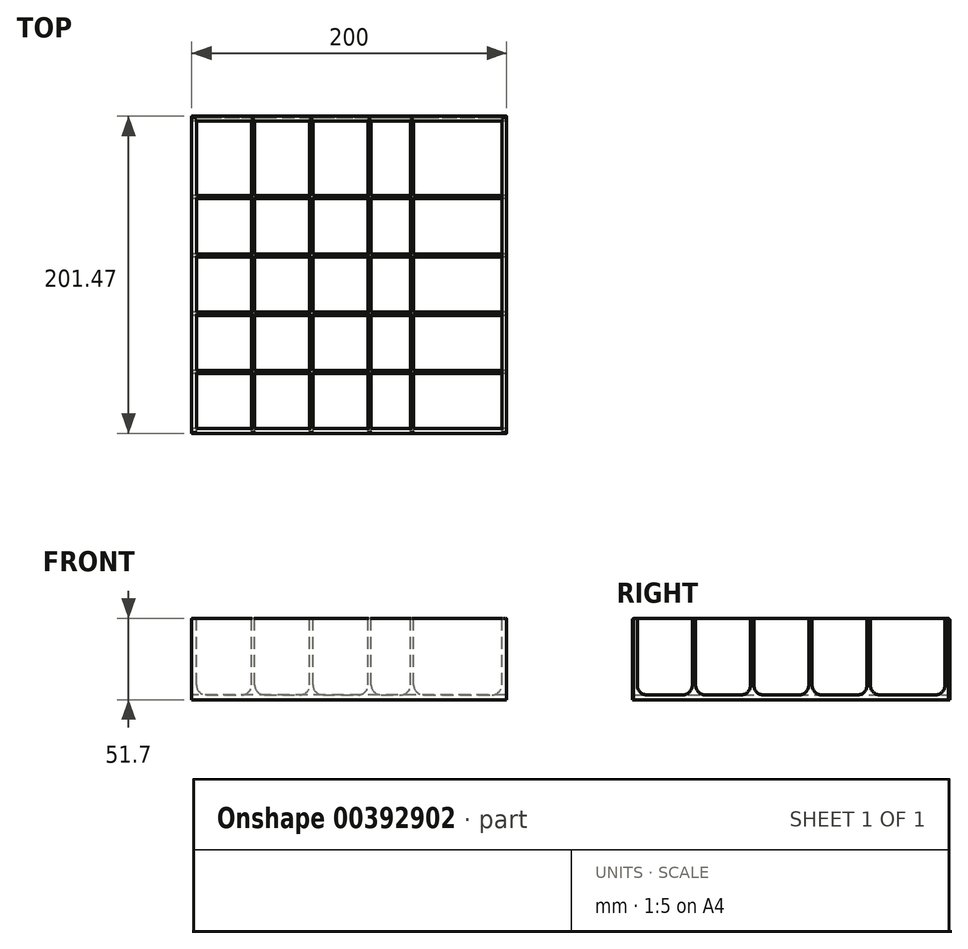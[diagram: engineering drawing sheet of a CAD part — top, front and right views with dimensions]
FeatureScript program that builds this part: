
annotation { "Feature Type Name" : "Feature", "Feature Type Description" : "" }
export const myFeature = defineFeature(function(context is Context, id is Id, definition is map)
    precondition{}
    {
        {
            var Q0;
            Q0=qCreatedBy(makeId("Front.planeOp"),FACE);
            var sketch = newSketch(context, id + "F0", { "sketchPlane" : qUnion([Q0])});
            skLineSegment(sketch, "E0.bottom", {"start": v(-90.65, -22.35) * mm, "end": v(-68.35, -22.35) * mm});
            skLineSegment(sketch, "E0.top", {"start": v(-100, -25.4) * mm, "end": v(100, -25.4) * mm});
            skLineSegment(sketch, "E1.top", {"start": v(-99.1, 26.3) * mm, "end": v(-97.9, 26.3) * mm});
            skLineSegment(sketch, "E1.left", {"start": v(-100, -25.4) * mm, "end": v(-100, 25.4) * mm});
            skLineSegment(sketch, "E1.right", {"start": v(-97, -16) * mm, "end": v(-97, 25.4) * mm});
            skLineSegment(sketch, "E2.top", {"start": v(99.1, 26.3) * mm, "end": v(97.9, 26.3) * mm});
            skLineSegment(sketch, "E2.left", {"start": v(100, -25.4) * mm, "end": v(100, 25.4) * mm});
            skLineSegment(sketch, "E2.right", {"start": v(97, -16) * mm, "end": v(97, 25.4) * mm});
            skLineSegment(sketch, "E3.top", {"start": v(-61.1, 26.3) * mm, "end": v(-60.9, 26.3) * mm});
            skLineSegment(sketch, "E3.left", {"start": v(-62, -16) * mm, "end": v(-62, 25.4) * mm});
            skLineSegment(sketch, "E3.right", {"start": v(-60, -16) * mm, "end": v(-60, 25.4) * mm});
            skLineSegment(sketch, "E4.top", {"start": v(-24.1, 26.3) * mm, "end": v(-23.9, 26.3) * mm});
            skLineSegment(sketch, "E4.left", {"start": v(-25, -16) * mm, "end": v(-25, 25.4) * mm});
            skLineSegment(sketch, "E4.right", {"start": v(-23, -16) * mm, "end": v(-23, 25.4) * mm});
            skLineSegment(sketch, "E5.top", {"start": v(12.9, 26.3) * mm, "end": v(13.1, 26.3) * mm});
            skLineSegment(sketch, "E5.left", {"start": v(12, -16) * mm, "end": v(12, 25.4) * mm});
            skLineSegment(sketch, "E5.right", {"start": v(14, -16) * mm, "end": v(14, 25.4) * mm});
            skLineSegment(sketch, "E6.top", {"start": v(39.9, 26.3) * mm, "end": v(40.1, 26.3) * mm});
            skLineSegment(sketch, "E6.left", {"start": v(39, -16) * mm, "end": v(39, 25.4) * mm});
            skLineSegment(sketch, "E6.right", {"start": v(41, -16) * mm, "end": v(41, 25.4) * mm});
            skArc(sketch, "E7.filletArc", {"start": v(-97, -16) * mm, "mid": v(-95.14, -20.49) * mm, "end": v(-90.65, -22.35) * mm});
            skArc(sketch, "E8.filletArc", {"start": v(-68.35, -22.35) * mm, "mid": v(-63.86, -20.49) * mm, "end": v(-62, -16) * mm});
            skLineSegment(sketch, "E9", {"start": v(-53.65, -22.35) * mm, "end": v(-31.35, -22.35) * mm});
            skArc(sketch, "E10.filletArc", {"start": v(-60, -16) * mm, "mid": v(-58.14, -20.49) * mm, "end": v(-53.65, -22.35) * mm});
            skArc(sketch, "E11.filletArc", {"start": v(-31.35, -22.35) * mm, "mid": v(-26.86, -20.49) * mm, "end": v(-25, -16) * mm});
            skLineSegment(sketch, "E12", {"start": v(20.35, -22.35) * mm, "end": v(32.65, -22.35) * mm});
            skLineSegment(sketch, "E13", {"start": v(47.35, -22.35) * mm, "end": v(90.65, -22.35) * mm});
            skLineSegment(sketch, "E14", {"start": v(-16.65, -22.35) * mm, "end": v(5.65, -22.35) * mm});
            skArc(sketch, "E15.filletArc", {"start": v(-23, -16) * mm, "mid": v(-21.14, -20.49) * mm, "end": v(-16.65, -22.35) * mm});
            skArc(sketch, "E16.filletArc", {"start": v(5.65, -22.35) * mm, "mid": v(10.14, -20.49) * mm, "end": v(12, -16) * mm});
            skArc(sketch, "E17.filletArc", {"start": v(14, -16) * mm, "mid": v(15.86, -20.49) * mm, "end": v(20.35, -22.35) * mm});
            skArc(sketch, "E18.filletArc", {"start": v(32.65, -22.35) * mm, "mid": v(37.14, -20.49) * mm, "end": v(39, -16) * mm});
            skArc(sketch, "E19.filletArc", {"start": v(41, -16) * mm, "mid": v(42.86, -20.49) * mm, "end": v(47.35, -22.35) * mm});
            skArc(sketch, "E20.filletArc", {"start": v(90.65, -22.35) * mm, "mid": v(95.14, -20.49) * mm, "end": v(97, -16) * mm});
            skPoint(sketch, "E21.visualSharp", {"position": v(-100, 26.3) * mm});
            skArc(sketch, "E21.filletArc", {"start": v(-99.1, 26.3) * mm, "mid": v(-99.74, 26.04) * mm, "end": v(-100, 25.4) * mm});
            skPoint(sketch, "E22.visualSharp", {"position": v(-97, 26.3) * mm});
            skArc(sketch, "E22.filletArc", {"start": v(-97, 25.4) * mm, "mid": v(-97.26, 26.04) * mm, "end": v(-97.9, 26.3) * mm});
            skPoint(sketch, "E23.visualSharp", {"position": v(-62, 26.3) * mm});
            skArc(sketch, "E23.filletArc", {"start": v(-61.1, 26.3) * mm, "mid": v(-61.74, 26.04) * mm, "end": v(-62, 25.4) * mm});
            skPoint(sketch, "E24.visualSharp", {"position": v(-60, 26.3) * mm});
            skArc(sketch, "E24.filletArc", {"start": v(-60, 25.4) * mm, "mid": v(-60.26, 26.04) * mm, "end": v(-60.9, 26.3) * mm});
            skPoint(sketch, "E25.visualSharp", {"position": v(-25, 26.3) * mm});
            skArc(sketch, "E25.filletArc", {"start": v(-24.1, 26.3) * mm, "mid": v(-24.74, 26.04) * mm, "end": v(-25, 25.4) * mm});
            skPoint(sketch, "E26.visualSharp", {"position": v(-23, 26.3) * mm});
            skArc(sketch, "E26.filletArc", {"start": v(-23, 25.4) * mm, "mid": v(-23.26, 26.04) * mm, "end": v(-23.9, 26.3) * mm});
            skPoint(sketch, "E27.visualSharp", {"position": v(12, 26.3) * mm});
            skArc(sketch, "E27.filletArc", {"start": v(12.9, 26.3) * mm, "mid": v(12.26, 26.04) * mm, "end": v(12, 25.4) * mm});
            skPoint(sketch, "E28.visualSharp", {"position": v(14, 26.3) * mm});
            skArc(sketch, "E28.filletArc", {"start": v(14, 25.4) * mm, "mid": v(13.74, 26.04) * mm, "end": v(13.1, 26.3) * mm});
            skPoint(sketch, "E29.visualSharp", {"position": v(39, 26.3) * mm});
            skArc(sketch, "E29.filletArc", {"start": v(39.9, 26.3) * mm, "mid": v(39.26, 26.04) * mm, "end": v(39, 25.4) * mm});
            skPoint(sketch, "E30.visualSharp", {"position": v(41, 26.3) * mm});
            skArc(sketch, "E30.filletArc", {"start": v(41, 25.4) * mm, "mid": v(40.74, 26.04) * mm, "end": v(40.1, 26.3) * mm});
            skPoint(sketch, "E31.visualSharp", {"position": v(97, 26.3) * mm});
            skArc(sketch, "E31.filletArc", {"start": v(97.9, 26.3) * mm, "mid": v(97.26, 26.04) * mm, "end": v(97, 25.4) * mm});
            skArc(sketch, "E32.filletArc", {"start": v(100, 25.4) * mm, "mid": v(99.74, 26.04) * mm, "end": v(99.1, 26.3) * mm});
            skSolve(sketch);
        }
        {
            var Q0;
            Q0=qCreatedBy(makeId("Right.planeOp"),FACE);
            var sketch = newSketch(context, id + "F1", { "sketchPlane" : qUnion([Q0])});
            skLineSegment(sketch, "E33", {"start": v(99.33, -25.4) * mm, "end": v(-100.67, -25.4) * mm});
            skLineSegment(sketch, "E34", {"start": v(-100.67, -25.4) * mm, "end": v(-100.67, 25.4) * mm});
            skLineSegment(sketch, "E35", {"start": v(-99.9, 26.16) * mm, "end": v(-98.43, 26.16) * mm});
            skLineSegment(sketch, "E36", {"start": v(-97.67, 25.4) * mm, "end": v(-97.67, -16.05) * mm});
            skLineSegment(sketch, "E37", {"start": v(-91.32, -22.4) * mm, "end": v(-69.02, -22.4) * mm});
            skLineSegment(sketch, "E38", {"start": v(97.8, -16.05) * mm, "end": v(97.8, 25.4) * mm});
            skLineSegment(sketch, "E39", {"start": v(98.56, 26.16) * mm, "end": v(100.04, 26.16) * mm});
            skLineSegment(sketch, "E40", {"start": v(100.8, 25.4) * mm, "end": v(100.8, -25.4) * mm});
            skLineSegment(sketch, "E41", {"start": v(-62.67, -16.05) * mm, "end": v(-62.67, 25.4) * mm});
            skLineSegment(sketch, "E42", {"start": v(-61.9, 26.16) * mm, "end": v(-61.43, 26.16) * mm});
            skLineSegment(sketch, "E43", {"start": v(-60.67, 25.4) * mm, "end": v(-60.67, -16.05) * mm});
            skLineSegment(sketch, "E44.bottom", {"start": v(-24.9, 26.16) * mm, "end": v(-24.43, 26.16) * mm});
            skLineSegment(sketch, "E44.top", {"start": v(-25.67, -22.4) * mm, "end": v(-23.67, -22.4) * mm});
            skLineSegment(sketch, "E44.left", {"start": v(-25.67, 25.4) * mm, "end": v(-25.67, -16.05) * mm});
            skLineSegment(sketch, "E44.right", {"start": v(-23.67, 25.4) * mm, "end": v(-23.67, -16.05) * mm});
            skLineSegment(sketch, "E45.bottom", {"start": v(12.1, 26.16) * mm, "end": v(12.57, 26.16) * mm});
            skLineSegment(sketch, "E45.top", {"start": v(11.33, -22.4) * mm, "end": v(13.33, -22.4) * mm});
            skLineSegment(sketch, "E45.left", {"start": v(11.33, 25.4) * mm, "end": v(11.33, -16.05) * mm});
            skLineSegment(sketch, "E45.right", {"start": v(13.33, 25.4) * mm, "end": v(13.33, -16.05) * mm});
            skLineSegment(sketch, "E46.bottom", {"start": v(49.1, 26.16) * mm, "end": v(49.57, 26.16) * mm});
            skLineSegment(sketch, "E46.left", {"start": v(48.33, 25.4) * mm, "end": v(48.33, -16.05) * mm});
            skLineSegment(sketch, "E46.right", {"start": v(50.33, 25.4) * mm, "end": v(50.33, -16.05) * mm});
            skPoint(sketch, "E47.visualSharp", {"position": v(-97.67, -22.4) * mm});
            skArc(sketch, "E47.filletArc", {"start": v(-97.67, -16.05) * mm, "mid": v(-95.81, -20.54) * mm, "end": v(-91.32, -22.4) * mm});
            skArc(sketch, "E48.filletArc", {"start": v(-69.02, -22.4) * mm, "mid": v(-64.53, -20.54) * mm, "end": v(-62.67, -16.05) * mm});
            skLineSegment(sketch, "E49", {"start": v(-54.32, -22.4) * mm, "end": v(-32.02, -22.4) * mm});
            skLineSegment(sketch, "E50", {"start": v(-17.32, -22.4) * mm, "end": v(4.98, -22.4) * mm});
            skLineSegment(sketch, "E51", {"start": v(56.68, -22.4) * mm, "end": v(91.45, -22.4) * mm});
            skLineSegment(sketch, "E52", {"start": v(19.68, -22.4) * mm, "end": v(41.98, -22.4) * mm});
            skPoint(sketch, "E53.visualSharp", {"position": v(-60.67, -22.4) * mm});
            skArc(sketch, "E53.filletArc", {"start": v(-60.67, -16.05) * mm, "mid": v(-58.81, -20.54) * mm, "end": v(-54.32, -22.4) * mm});
            skPoint(sketch, "E54.visualSharp", {"position": v(-25.67, -22.4) * mm});
            skArc(sketch, "E54.filletArc", {"start": v(-32.02, -22.4) * mm, "mid": v(-27.53, -20.54) * mm, "end": v(-25.67, -16.05) * mm});
            skPoint(sketch, "E55.visualSharp", {"position": v(-23.67, -22.4) * mm});
            skArc(sketch, "E55.filletArc", {"start": v(-23.67, -16.05) * mm, "mid": v(-21.81, -20.54) * mm, "end": v(-17.32, -22.4) * mm});
            skPoint(sketch, "E56.visualSharp", {"position": v(11.33, -22.4) * mm});
            skArc(sketch, "E56.filletArc", {"start": v(4.98, -22.4) * mm, "mid": v(9.47, -20.54) * mm, "end": v(11.33, -16.05) * mm});
            skPoint(sketch, "E57.visualSharp", {"position": v(13.33, -22.4) * mm});
            skArc(sketch, "E57.filletArc", {"start": v(13.33, -16.05) * mm, "mid": v(15.19, -20.54) * mm, "end": v(19.68, -22.4) * mm});
            skPoint(sketch, "E58.visualSharp", {"position": v(48.33, -22.4) * mm});
            skArc(sketch, "E58.filletArc", {"start": v(41.98, -22.4) * mm, "mid": v(46.47, -20.54) * mm, "end": v(48.33, -16.05) * mm});
            skPoint(sketch, "E59.visualSharp", {"position": v(50.33, -22.4) * mm});
            skArc(sketch, "E59.filletArc", {"start": v(50.33, -16.05) * mm, "mid": v(52.19, -20.54) * mm, "end": v(56.68, -22.4) * mm});
            skPoint(sketch, "E60.visualSharp", {"position": v(97.8, -22.4) * mm});
            skArc(sketch, "E60.filletArc", {"start": v(91.45, -22.4) * mm, "mid": v(95.94, -20.54) * mm, "end": v(97.8, -16.05) * mm});
            skPoint(sketch, "E61.visualSharp", {"position": v(-100.67, 26.16) * mm});
            skArc(sketch, "E61.filletArc", {"start": v(-99.9, 26.16) * mm, "mid": v(-100.45, 25.94) * mm, "end": v(-100.67, 25.4) * mm});
            skPoint(sketch, "E62.visualSharp", {"position": v(-97.67, 26.16) * mm});
            skArc(sketch, "E62.filletArc", {"start": v(-97.67, 25.4) * mm, "mid": v(-97.9, 25.94) * mm, "end": v(-98.43, 26.16) * mm});
            skPoint(sketch, "E63.visualSharp", {"position": v(-62.67, 26.16) * mm});
            skArc(sketch, "E63.filletArc", {"start": v(-61.9, 26.16) * mm, "mid": v(-62.45, 25.94) * mm, "end": v(-62.67, 25.4) * mm});
            skPoint(sketch, "E64.visualSharp", {"position": v(-60.67, 26.16) * mm});
            skArc(sketch, "E64.filletArc", {"start": v(-60.67, 25.4) * mm, "mid": v(-60.9, 25.94) * mm, "end": v(-61.43, 26.16) * mm});
            skPoint(sketch, "E65.visualSharp", {"position": v(-25.67, 26.16) * mm});
            skArc(sketch, "E65.filletArc", {"start": v(-24.9, 26.16) * mm, "mid": v(-25.45, 25.94) * mm, "end": v(-25.67, 25.4) * mm});
            skPoint(sketch, "E66.visualSharp", {"position": v(-23.67, 26.16) * mm});
            skArc(sketch, "E66.filletArc", {"start": v(-23.67, 25.4) * mm, "mid": v(-23.9, 25.94) * mm, "end": v(-24.43, 26.16) * mm});
            skPoint(sketch, "E67.visualSharp", {"position": v(11.33, 26.16) * mm});
            skArc(sketch, "E67.filletArc", {"start": v(12.1, 26.16) * mm, "mid": v(11.55, 25.94) * mm, "end": v(11.33, 25.4) * mm});
            skPoint(sketch, "E68.visualSharp", {"position": v(13.33, 26.16) * mm});
            skArc(sketch, "E68.filletArc", {"start": v(13.33, 25.4) * mm, "mid": v(13.1, 25.94) * mm, "end": v(12.57, 26.16) * mm});
            skPoint(sketch, "E69.visualSharp", {"position": v(48.33, 26.16) * mm});
            skArc(sketch, "E69.filletArc", {"start": v(49.1, 26.16) * mm, "mid": v(48.55, 25.94) * mm, "end": v(48.33, 25.4) * mm});
            skPoint(sketch, "E70.visualSharp", {"position": v(50.33, 26.16) * mm});
            skArc(sketch, "E70.filletArc", {"start": v(50.33, 25.4) * mm, "mid": v(50.1, 25.94) * mm, "end": v(49.57, 26.16) * mm});
            skPoint(sketch, "E71.visualSharp", {"position": v(97.8, 26.16) * mm});
            skArc(sketch, "E71.filletArc", {"start": v(98.56, 26.16) * mm, "mid": v(98.02, 25.94) * mm, "end": v(97.8, 25.4) * mm});
            skPoint(sketch, "E72.visualSharp", {"position": v(100.8, 26.16) * mm});
            skArc(sketch, "E72.filletArc", {"start": v(100.8, 25.4) * mm, "mid": v(100.58, 25.94) * mm, "end": v(100.04, 26.16) * mm});
            skLineSegment(sketch, "E73", {"start": v(99.33, -25.4) * mm, "end": v(100.8, -25.4) * mm});
            skSolve(sketch);
        }
        {
            var Q0;
            Q0 = qSketchRegion(id + "F0", true);
            extrude(context, id + "F2", {"entities" : qUnion([Q0]), "endBound" : BoundingType.SYMMETRIC, "depth" : 200 * mm});
        }
        {
            var Q0;
            Q0 = qSketchRegion(id + "F1", true);
            extrude(context, id + "F3", {"entities" : qUnion([Q0]), "endBound" : BoundingType.SYMMETRIC, "depth" : 200 * mm});
        }
    });
